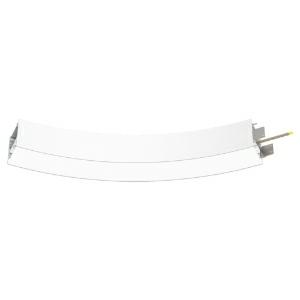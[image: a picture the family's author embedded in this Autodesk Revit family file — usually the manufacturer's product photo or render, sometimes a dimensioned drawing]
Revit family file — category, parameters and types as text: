
# Revit family: super-g_slim_super_g_slim_dir_ind_1550_45deg_hl_ps_led_18w__2880lm__3000k__cri80_430-3740_a04b
name_source: partatom
category: Leuchten
revit_build: Autodesk Revit 2016 (Build: 20190508_0715(x64)
units: mm (PartAtom-declared; Revit-internal decimal feet)

## family parameters
Basisbauteil = Fläche
Beim Laden mit Abzugskörper schneiden = Nein
Bemaßung runder Anschluss = Durchmesser verwenden
Gemeinsam genutzt = Nein
Lichtquelle = Nein
Raumberechnungspunkt = Nein
Teiletyp = Normal

## types (1)
- 430-3740-D01 (1 x LED, 720 lm, 3000K)
    Beschreibung = The insert consists of aluminum-extruded profile. Charming SOFT-EDGE design ensure unparalleled styling. The ballast is integrated and allows for an operation with 220-240V (50/60Hz). SUPER-G (# 430-3740) ist not dimmable (on/off).
    CIE Flux Codes = 48 79 96 66 85
    Color Rendering = 1B/80…89
    Color Temperature = 3000K
    Height = 90 mm
    Hersteller = Prolicht
    Lamp Light Flux = 720 lm
    Lamp count = 1
    Lampe = 1 x LED
    Length = 146 mm
    Luminous efficacy = 122 lm/W
    ModVariant = Nein
    Modell = 430-3740
    Mounting Place = Ceiling
    Mounting Type = Pendant
    Number of Poles = 1
    OnlyDefault = Ja
    Power Factor = 1
    Product Name = SUPER-G SLIM__SUPER G SLIM DIR/IND 1550/45° HL PS LED 18W  2880lm  3000K  CRI80
    Product group = Suspended profile systems
    ProductGroupID = 944
    Protection Class = Protection class
    Protection Degree = Degree of protection
    RLX_Detail_Level = 1
    RlxData = <blob elided: 31389 chars, md5=db0befab>
    Scheinlast = 20 VA
    Socket = socket
    Standby Power = 0 W
    System Light Flux = 2436 lm
    System Power = 20 W
    Typenbild = 430-3740.jpg
    URL = http://relux.com
    VarID = 430-3740-d01
    Voltage = 0 V
    Vorgabe-Ansicht = 1800 mm
    Weight = 0.00 kg
    Width = 65 mm

## geometry (parser evidence)
native form markers: Blend x4, Sweep x25
no freeform markers — native parametric forms only
